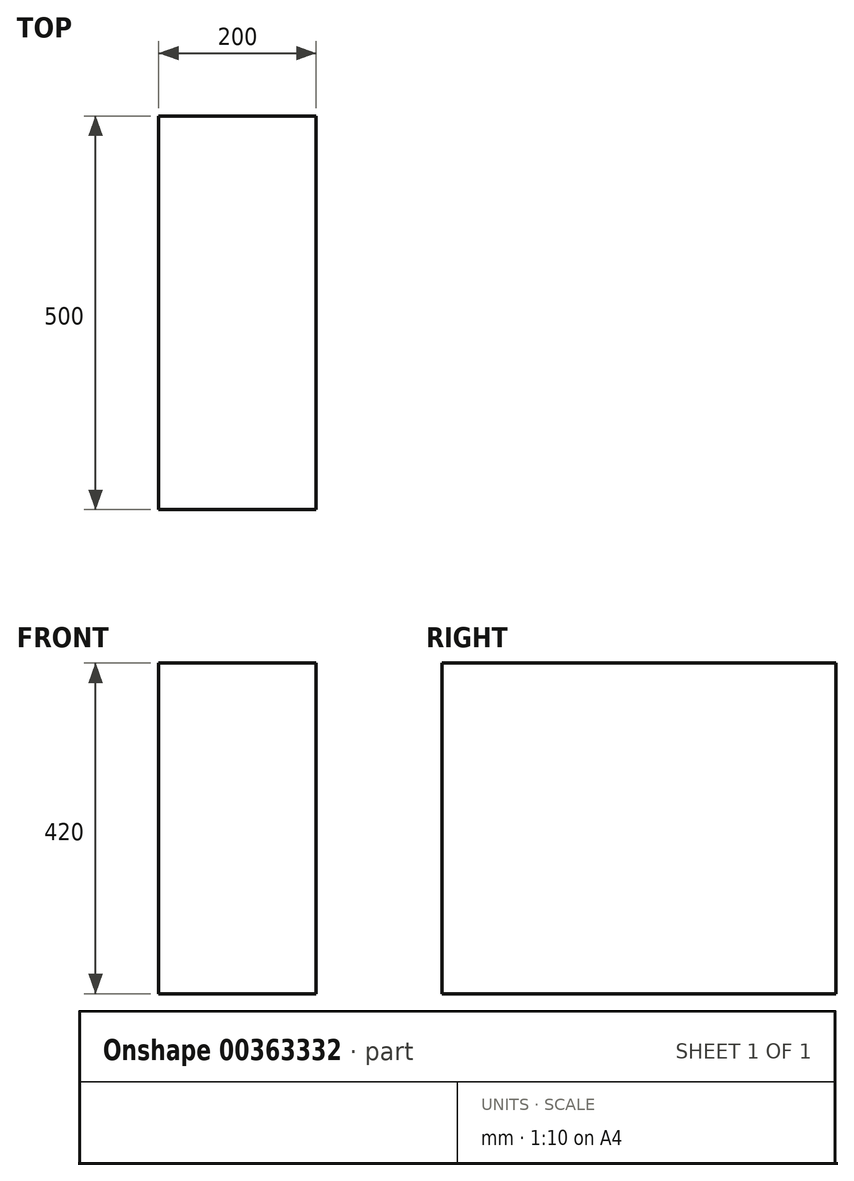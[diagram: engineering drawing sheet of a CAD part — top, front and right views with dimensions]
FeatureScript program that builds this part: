
annotation { "Feature Type Name" : "Feature", "Feature Type Description" : "" }
export const myFeature = defineFeature(function(context is Context, id is Id, definition is map)
    precondition{}
    {
        {
            var Q0;
            Q0=qCreatedBy(makeId("Top.planeOp"),FACE);
            var sketch = newSketch(context, id + "F0", { "sketchPlane" : qUnion([Q0])});
            skLineSegment(sketch, "E0.bottom", {"start": v(0, 0) * mm, "end": v(200, 0) * mm});
            skLineSegment(sketch, "E0.top", {"start": v(0, 500) * mm, "end": v(200, 500) * mm});
            skLineSegment(sketch, "E0.left", {"start": v(0, 0) * mm, "end": v(0, 500) * mm});
            skLineSegment(sketch, "E0.right", {"start": v(200, 0) * mm, "end": v(200, 500) * mm});
            skSolve(sketch);
        }
        {
            var Q0;
            Q0=makeQuery(id+"F0.imprint","IMPRINT",FACE,{"disambiguationData":[TD([[makeQuery(id+"F0.imprint","IMPRINT",EDGE,{"derivedFrom":sQuery(id+"F0.wireOp",EDGE,"E0.bottom")}),1.0]])]});
            extrude(context, id + "F1", {"entities" : qUnion([Q0]), "depth" : 420 * mm});
        }
    });
